# Revit family: LAMP_BAULINE G3 AIR
name_source: partatom
category: Modelos genéricos
revit_build: Autodesk Revit 2018 (Build: 20190510_1515(x64)
units: mm (PartAtom-declared; Revit-internal decimal feet)

## family parameters
Anfitrión = Cara
Compartido = No
Corte con vacíos al cargar = No
Cota de conector redondo = Diámetro de uso
Puede alojar armadura = No
Punto de cálculo de habitación = No
Tipo de pieza = Normal

## types (12) — shared parameters
CRI = 80
Comentarios de tipo = Availability of tilting between 0º and 30º when placed in a project.
Descripción = BAULINE G2 AIR 2500 WW SP AND.
Dimensions = 650x50x95
Elevación por defecto = 1219 mm
Fabricante = LAMP
Finish = Anodized matte silver
Gear = Electronic
Height = 95 mm
Initial intensity = 1940 lm
Installation instructions = https://www.lamp.es
Insulation class = I
LED Lifetime = 83.000 L90 B10
Lamp = HIGH POWER LED
Last update = 09/02/2022
Luminaire type = Outdoor - Surface luminaire
MacAdam = 3
Manufacturer URL = http://www.lamp.es
Manufacturer country = Spain
Manufacturer name = LAMP
Model explanation = Availability of tilting between 0º and 30º when placed in a project.
Power Supply = 220-240V 50/60Hz
Product URL = https://www.lamp.es
Product datasheet = http://www.lamp.es
Protection rating = IP67 / IK10
Type = HIGH POWER NICHIA

## per-type parameters (varying)
| type | Efficacy | Initial color | Modelo | Photometric web file | Plum | Power | Product code | Weight |
| 1792LM 3000 MEDIUM FLOOD | 126 lm/W | 3000 K | BA3SF065MOMF830NG | Cuerpo Bauline Air G3 : 1792LM 3000 MEDIUM FLOOD | 16 W | 16 W | BA3SF065MOMF830NG | 2.25 kg |
| 1916LM 3000 ELLIPTIC | 121 lm/W | 3000 K | BA3SF065MOEL830NG | Cuerpo Bauline Air G3 : 1916LM 3000 ELLIPTIC | 16 W | 16 W | BA3SF065MOEL830NG | 2.25 kg |
| 1916LM 4000 ELLIPTIC | 121 lm/W | 4000 K | BA3SF065MOEL840NG | Cuerpo Bauline Air G3 : 1916LM 4000 ELLIPTIC | 16 W | 16 W | BA3SF065MOEL840NG | 2.25 kg |
| 1937LM 3000 SPOT | 124 lm/W | 3000 K | BA3SF065MOSP830NG | Cuerpo Bauline Air G3 : 1937LM 3000 SPOT | 16 W | 16 W | BA3SF065MOSP830NG | 2.25 kg |
| 1937LM 4000 SPOT | 124 lm/W | 4000 K | BA3SF065MOSP840NG | Cuerpo Bauline Air G3 : 1937LM 4000 SPOT | 16 W | 16 W | BA3SF065MOSP840NG | 2.25 kg |
| 1972LM 4000 MEDIUM FLOOD | 126 lm/W | 4000 K | BA3SF065MOMF840NG | Cuerpo Bauline Air G3 : 1972LM 4000 MEDIUM FLOOD | 16 W | 16 W | BA3SF065MOMF840NG | 2.25 kg |
| 3832LM 3000 ELLIPTIC | 119 lm/W | 3000 K | BA3SF124MOEL830NG | Cuerpo Bauline Air G3 : 3832LM 3000 ELLIPTIC | 32 W | 31 W | BA3SF124MOEL830NG | 3.38 kg |
| 3832LM 4000 ELLIPTIC | 119 lm/W | 4000 K | BA3SF124MOEL840NG | Cuerpo Bauline Air G3 : 3832LM 4000 ELLIPTIC | 32 W | 31 W | BA3SF124MOEL840NG | 3.38 kg |
| 3873LM 3000 SPOT | 121 lm/W | 3000 K | BA3SF124MOSP830NG | Cuerpo Bauline Air G3 : 3873LM 3000 SPOT | 32 W | 31 W | BA3SF124MOSP830NG | 3.38 kg |
| 3873LM 4000 SPOT | 121 lm/W | 4000 K | BA3SF124MOSP840NG | Cuerpo Bauline Air G3 : 3873LM 4000 SPOT | 32 W | 31 W | BA3SF124MOSP840NG | 3.38 kg |
| 3945LM 3000 MEDIUM FLOOD | 124 lm/W | 3000 K | BA3SF124MOMF830NG | Cuerpo Bauline Air G3 : 3945LM 3000 MEDIUM FLOOD | 32 W | 31 W | BA3SF124MOMF830NG | 3.38 kg |
| 3945LM 4000 MEDIUM FLOOD | 124 lm/W | 4000 K | BA3SF124MOMF840NG | Cuerpo Bauline Air G3 : 3945LM 4000 MEDIUM FLOOD | 32 W | 31 W | BA3SF124MOMF840NG | 3.38 kg |

## geometry (parser evidence)
native form markers: Blend x4
no freeform markers — native parametric forms only
